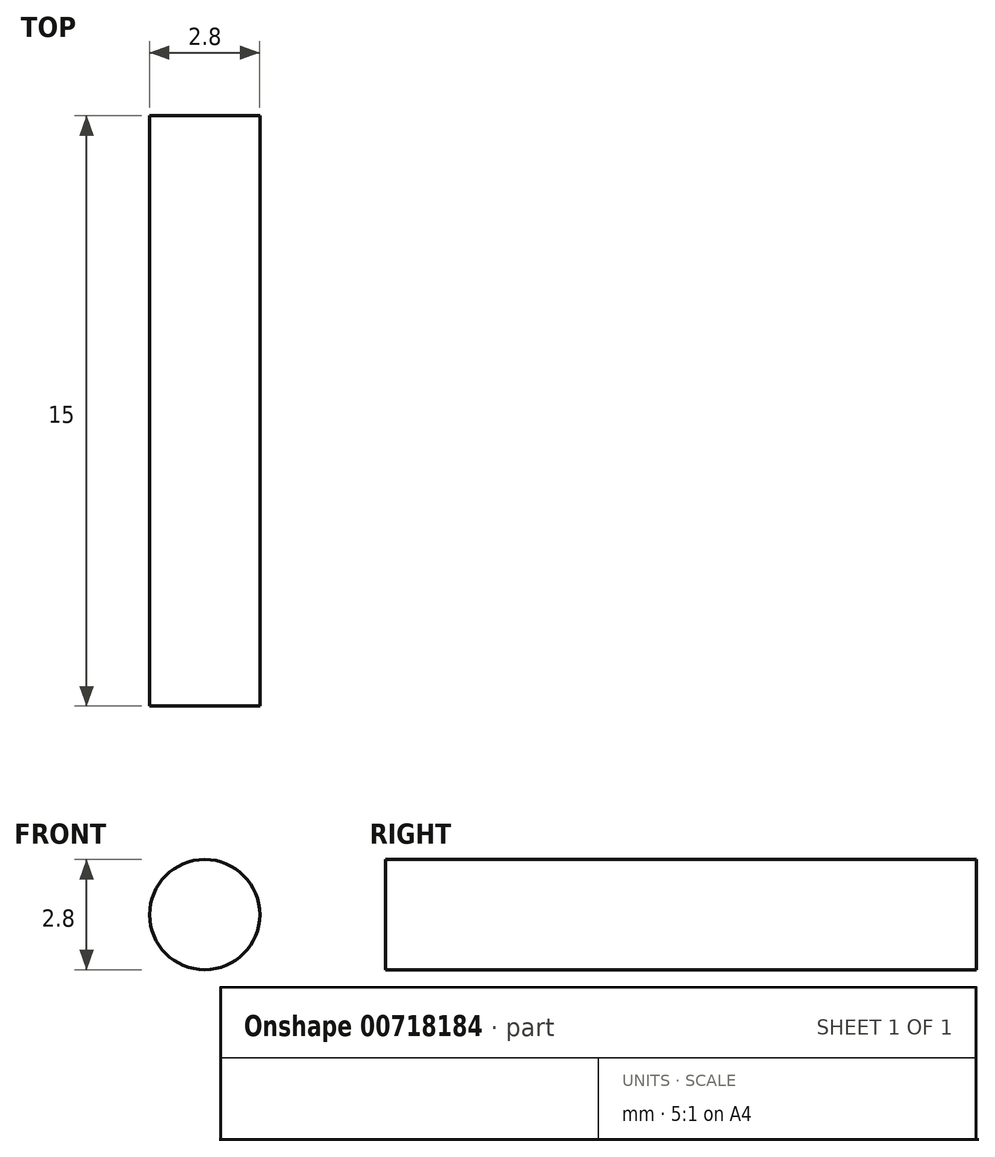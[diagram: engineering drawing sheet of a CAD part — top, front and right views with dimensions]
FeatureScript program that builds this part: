
annotation { "Feature Type Name" : "Feature", "Feature Type Description" : "" }
export const myFeature = defineFeature(function(context is Context, id is Id, definition is map)
    precondition{}
    {
        {
            var Q0;
            Q0=qCreatedBy(makeId("Front.planeOp"),FACE);
            var sketch = newSketch(context, id + "F0", { "sketchPlane" : qUnion([Q0])});
            skCircle(sketch, "E0", {"center": v(39.31, 25.5) * mm, "radius": 1.4 * mm});
            skSolve(sketch);
        }
        {
            var Q0;
            Q0=makeQuery(id+"F0.imprint","IMPRINT",FACE,{"disambiguationData":[TD([[makeQuery(id+"F0.imprint","IMPRINT",EDGE,{"derivedFrom":sQuery(id+"F0.wireOp",EDGE,"E0")}),1.0]])]});
            extrude(context, id + "F1", {"entities" : qUnion([Q0]), "depth" : 15 * mm, "offsetDistance" : 25 * mm});
        }
    });
